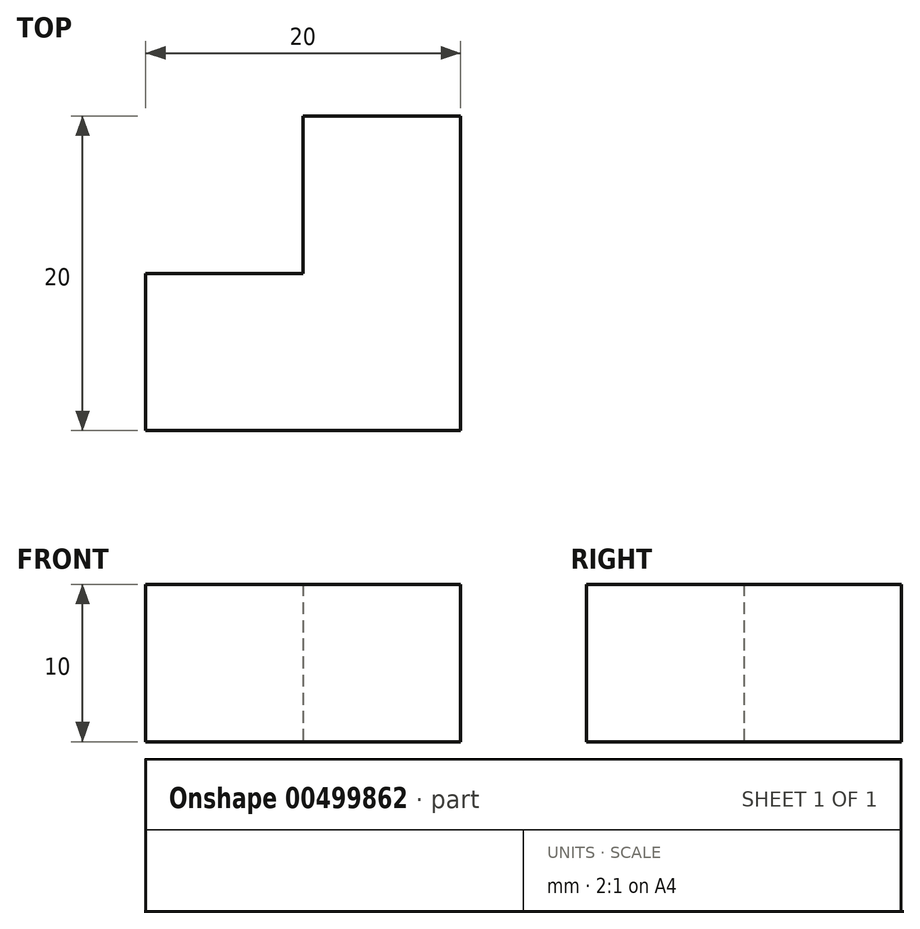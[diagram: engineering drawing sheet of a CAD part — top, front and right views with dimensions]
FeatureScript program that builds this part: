
annotation { "Feature Type Name" : "Feature", "Feature Type Description" : "" }
export const myFeature = defineFeature(function(context is Context, id is Id, definition is map)
    precondition{}
    {
        {
            var Q0;
            Q0=qCreatedBy(makeId("Top.planeOp"),FACE);
            var sketch = newSketch(context, id + "F0", { "sketchPlane" : qUnion([Q0])});
            skLineSegment(sketch, "E0", {"start": v(0, 0) * mm, "end": v(20, 0) * mm});
            skLineSegment(sketch, "E1", {"start": v(20, 20) * mm, "end": v(20, 0) * mm});
            skLineSegment(sketch, "E2", {"start": v(20, 20) * mm, "end": v(10, 20) * mm});
            skLineSegment(sketch, "E3", {"start": v(10, 20) * mm, "end": v(10, 10) * mm});
            skLineSegment(sketch, "E4", {"start": v(10, 10) * mm, "end": v(0, 10) * mm});
            skLineSegment(sketch, "E5", {"start": v(0, 10) * mm, "end": v(0, 0) * mm});
            skSolve(sketch);
        }
        {
            var Q0;
            Q0=makeQuery(id+"F0.imprint","IMPRINT",FACE,{"disambiguationData":[TD([[makeQuery(id+"F0.imprint","IMPRINT",EDGE,{"derivedFrom":sQuery(id+"F0.wireOp",EDGE,"E0")}),1.0]])]});
            extrude(context, id + "F1", {"entities" : qUnion([Q0]), "depth" : 10 * mm});
        }
    });
